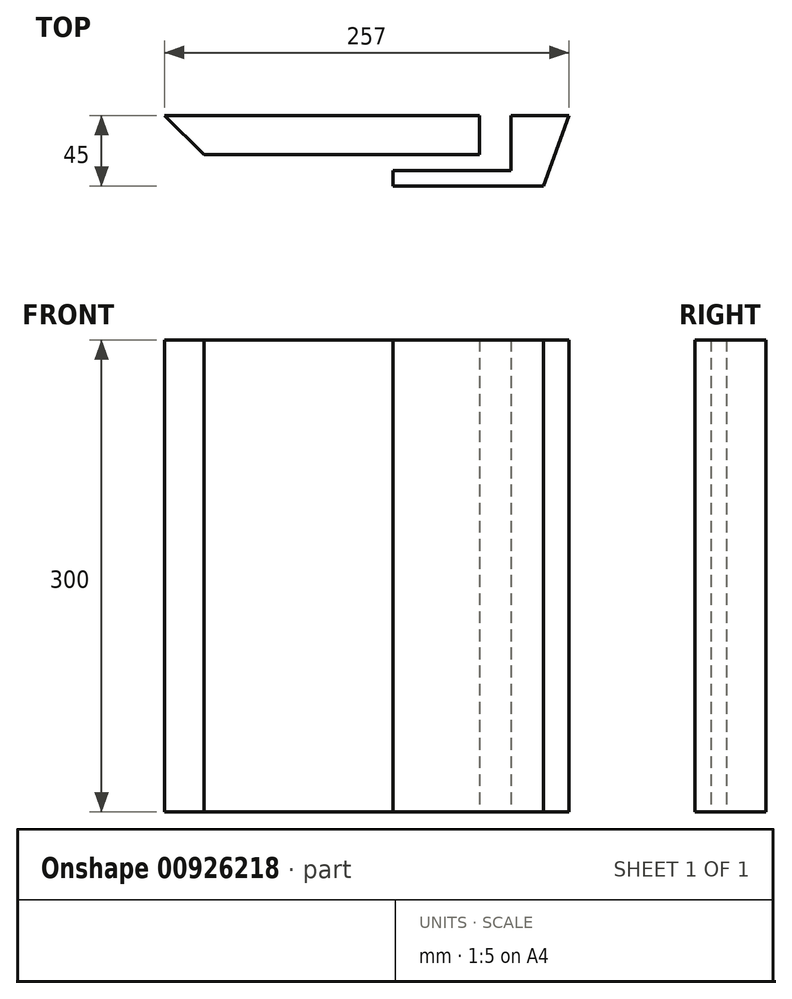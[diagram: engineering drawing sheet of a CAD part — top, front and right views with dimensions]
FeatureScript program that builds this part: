
annotation { "Feature Type Name" : "Feature", "Feature Type Description" : "" }
export const myFeature = defineFeature(function(context is Context, id is Id, definition is map)
    precondition{}
    {
        {
            var Q0;
            Q0=qCreatedBy(makeId("Top.planeOp"),FACE);
            var sketch = newSketch(context, id + "F0", { "sketchPlane" : qUnion([Q0])});
            skLineSegment(sketch, "E0", {"start": v(0, 22.73) * mm, "end": v(0, -55.3) * mm, "construction": true});
            skLineSegment(sketch, "E1", {"start": v(-200, 0) * mm, "end": v(0, 0) * mm});
            skLineSegment(sketch, "E2", {"start": v(0, 0) * mm, "end": v(0, -25) * mm});
            skLineSegment(sketch, "E3", {"start": v(0, -25) * mm, "end": v(-175, -25) * mm});
            skLineSegment(sketch, "E4", {"start": v(-175, -25) * mm, "end": v(-200, 0) * mm});
            skSolve(sketch);
        }
        {
            var Q0;
            Q0 = qSketchRegion(id + "F0", true);
            extrude(context, id + "F1", {"entities" : qUnion([Q0]), "depth" : 300 * mm, "offsetDistance" : 25 * mm});
        }
        {
            var Q0;
            Q0=qCreatedBy(makeId("Top.planeOp"),FACE);
            var sketch = newSketch(context, id + "F2", { "sketchPlane" : qUnion([Q0])});
            skLineSegment(sketch, "E5", {"start": v(20, 0) * mm, "end": v(20, -35) * mm});
            skLineSegment(sketch, "E6", {"start": v(20, -35) * mm, "end": v(-55, -35) * mm});
            skLineSegment(sketch, "E7", {"start": v(-55, -35) * mm, "end": v(-55, -45) * mm});
            skLineSegment(sketch, "E8", {"start": v(-55, -45) * mm, "end": v(40.62, -45) * mm});
            skLineSegment(sketch, "E9", {"start": v(40.62, -45) * mm, "end": v(57, 0) * mm});
            skLineSegment(sketch, "E10", {"start": v(57, 0) * mm, "end": v(20, 0) * mm});
            skSolve(sketch);
        }
        {
            var Q0;
            Q0 = qSketchRegion(id + "F2", true);
            extrude(context, id + "F3", {"entities" : qUnion([Q0]), "depth" : 300 * mm, "offsetDistance" : 25 * mm});
        }
    });
